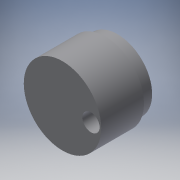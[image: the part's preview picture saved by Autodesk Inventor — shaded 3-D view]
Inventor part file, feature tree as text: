
AUTODESK INVENTOR PART (.ipt)
format: ipt  version: 2016 (Build 200138000, 138)  size: 110,592 bytes
history: native  units: in
note: dims shown in document units (in); Inventor stores cm internally (conversion verified against a paired STEP export)
features: extrude x3, reference x2, sketch x2
ambient origin geometry x8: Origin, YZ Plane, XZ Plane, XY Plane, X Axis, Y Axis, Z Axis, Center Point
bodies: Solid1 (feature_tree)
feature tree (7):
  extrude  "Extrusion1"  Depth=0.4134in TaperAngle=0.0deg
  extrude  "Extrusion2"  Depth=0.1181in
  extrude  "Extrusion3"  Depth=0.1969in TaperAngle=0.0deg
  reference  "Reference1"
  sketch  "Sketch2"  dims[d0=0.748in d1=0.4134in d2=0.0in]
  sketch  "Sketch3"  dims[d3=0.0984in d4=0.1673in d5=0.1969in d6=0.0in d7=0.6693in d8=0.1181in d9=0.0in]
  reference  "Reference2"
